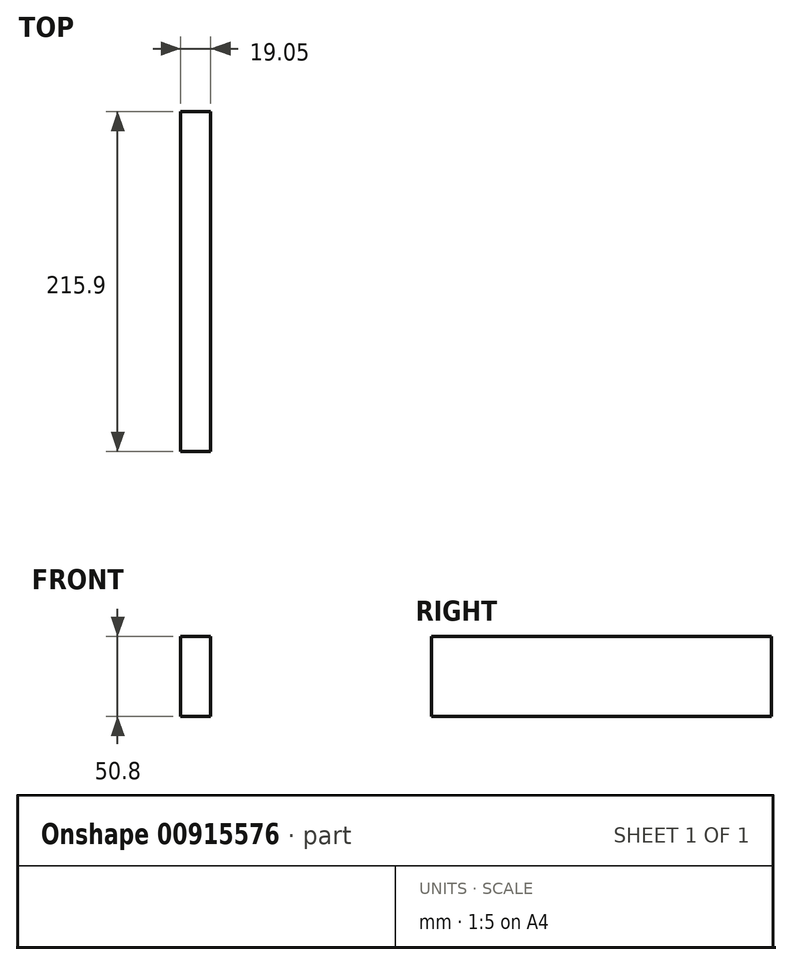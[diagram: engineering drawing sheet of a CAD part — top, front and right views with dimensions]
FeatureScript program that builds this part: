
annotation { "Feature Type Name" : "Feature", "Feature Type Description" : "" }
export const myFeature = defineFeature(function(context is Context, id is Id, definition is map)
    precondition{}
    {
        {
            var Q0;
            Q0=qCreatedBy(makeId("Right.planeOp"),FACE);
            var sketch = newSketch(context, id + "F0", { "sketchPlane" : qUnion([Q0])});
            skLineSegment(sketch, "E0.bottom", {"start": v(107.95, 25.4) * mm, "end": v(-107.95, 25.4) * mm});
            skLineSegment(sketch, "E0.top", {"start": v(107.95, -25.4) * mm, "end": v(-107.95, -25.4) * mm});
            skLineSegment(sketch, "E0.left", {"start": v(107.95, 25.4) * mm, "end": v(107.95, -25.4) * mm});
            skLineSegment(sketch, "E0.right", {"start": v(-107.95, 25.4) * mm, "end": v(-107.95, -25.4) * mm});
            skPoint(sketch, "E0.middle", {"position": v(0, 0) * mm});
            skSolve(sketch);
        }
        {
            var Q0;
            Q0=makeQuery(id+"F0.imprint","IMPRINT",FACE,{"disambiguationData":[TD([[makeQuery(id+"F0.imprint","IMPRINT",EDGE,{"derivedFrom":sQuery(id+"F0.wireOp",EDGE,"E0.bottom")}),1.0]])]});
            extrude(context, id + "F1", {"entities" : qUnion([Q0]), "depth" : 19.05 * mm, "offsetDistance" : 25.4 * mm});
        }
    });
